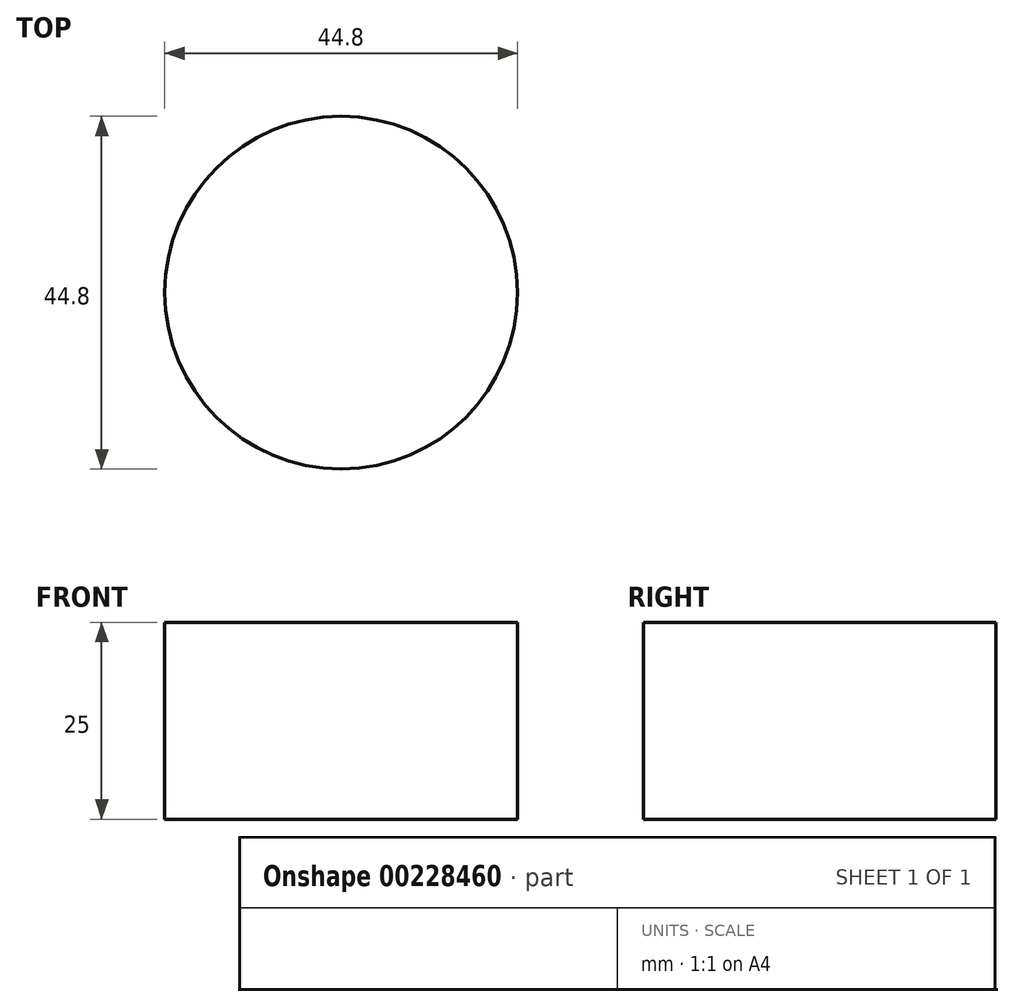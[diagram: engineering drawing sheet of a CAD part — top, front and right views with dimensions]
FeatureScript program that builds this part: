
annotation { "Feature Type Name" : "Feature", "Feature Type Description" : "" }
export const myFeature = defineFeature(function(context is Context, id is Id, definition is map)
    precondition{}
    {
        {
            var Q0;
            Q0=qCreatedBy(makeId("Top.planeOp"),FACE);
            var sketch = newSketch(context, id + "F0", { "sketchPlane" : qUnion([Q0])});
            skCircle(sketch, "E0", {"center": v(0, 0) * mm, "radius": 22.4 * mm});
            skSolve(sketch);
        }
        {
            var Q0;
            Q0=makeQuery(id+"F0.imprint","IMPRINT",FACE,{"disambiguationData":[TD([[makeQuery(id+"F0.imprint","IMPRINT",EDGE,{"derivedFrom":sQuery(id+"F0.wireOp",EDGE,"E0")}),1.0]])]});
            extrude(context, id + "F1", {"entities" : qUnion([Q0]), "oppositeDirection" : true, "depth" : 25 * mm});
        }
    });
